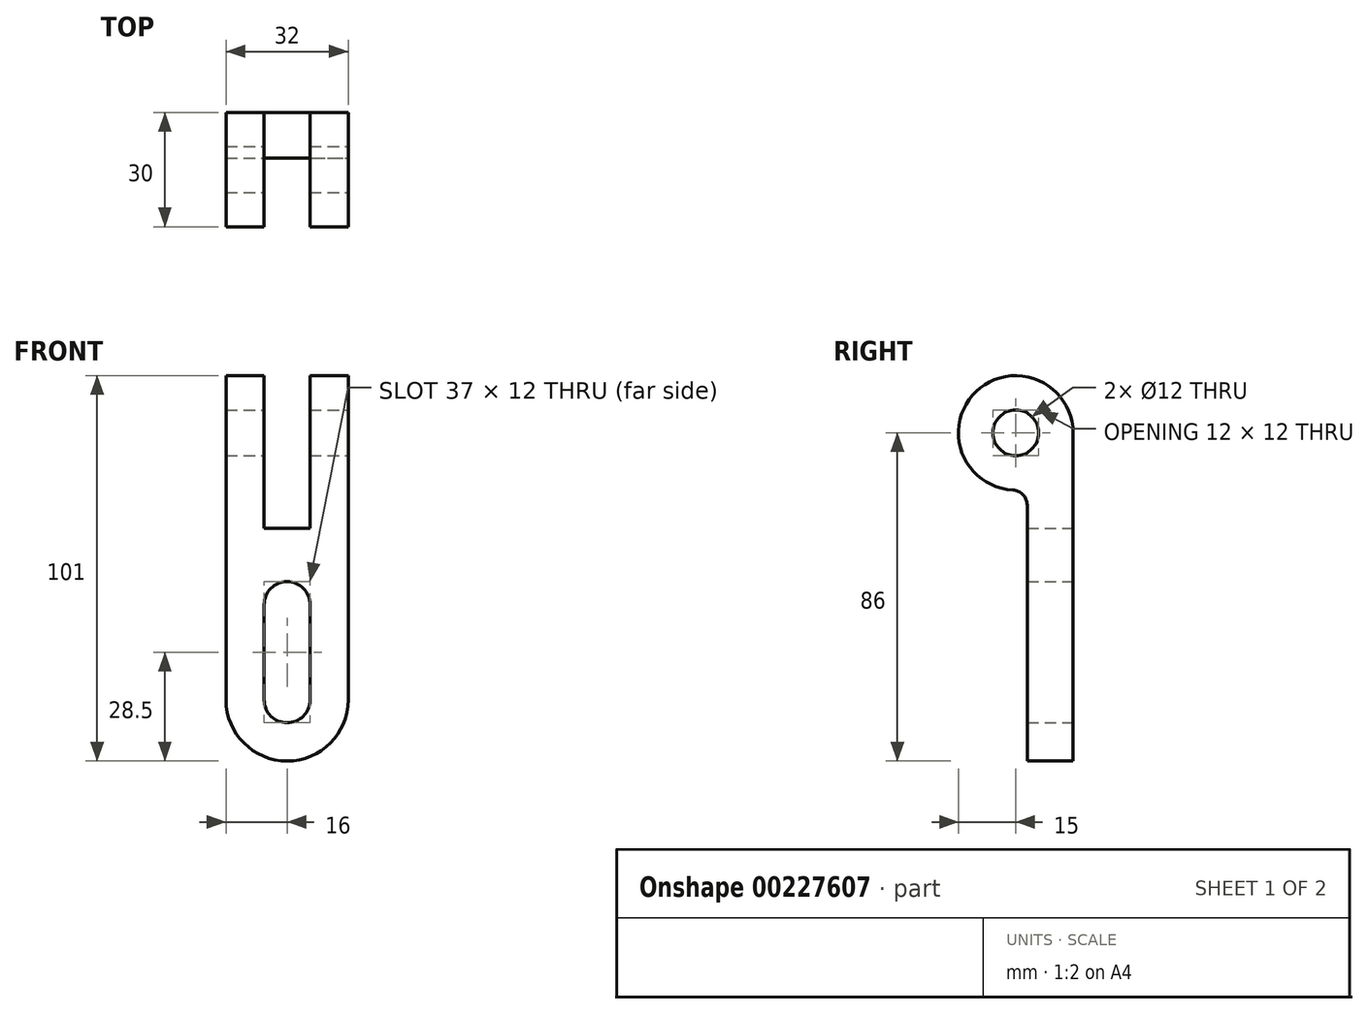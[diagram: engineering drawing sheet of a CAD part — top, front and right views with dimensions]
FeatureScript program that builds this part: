
annotation { "Feature Type Name" : "Feature", "Feature Type Description" : "" }
export const myFeature = defineFeature(function(context is Context, id is Id, definition is map)
    precondition{}
    {
        {
            var Q0;
            Q0=qCreatedBy(makeId("Front.planeOp"),FACE);
            var sketch = newSketch(context, id + "F0", { "sketchPlane" : qUnion([Q0])});
            skArc(sketch, "E0", {"start": v(-16, 0) * mm, "mid": v(-11.31, -11.31) * mm, "end": v(0, -16) * mm});
            skArc(sketch, "E1", {"start": v(-6, 0) * mm, "mid": v(-4.24, -4.24) * mm, "end": v(0, -6) * mm});
            skLineSegment(sketch, "E2", {"start": v(-16, 45) * mm, "end": v(-16, 0) * mm});
            skLineSegment(sketch, "E3", {"start": v(0, -30.56) * mm, "end": v(0, 67.76) * mm, "construction": true});
            skLineSegment(sketch, "E4", {"start": v(-23.42, 0) * mm, "end": v(30.75, 0) * mm, "construction": true});
            skArc(sketch, "E5", {"start": v(0, 31) * mm, "mid": v(-4.24, 29.24) * mm, "end": v(-6, 25) * mm});
            skLineSegment(sketch, "E6", {"start": v(-6, 0) * mm, "end": v(-6, 25) * mm});
            skArc(sketch, "E7.MirrorCS", {"start": v(0, 31) * mm, "mid": v(4.24, 29.24) * mm, "end": v(6, 25) * mm});
            skArc(sketch, "E8.MirrorCS", {"start": v(16, 0) * mm, "mid": v(11.31, -11.31) * mm, "end": v(0, -16) * mm});
            skArc(sketch, "E9.MirrorCS", {"start": v(6, 0) * mm, "mid": v(4.24, -4.24) * mm, "end": v(0, -6) * mm});
            skLineSegment(sketch, "E10.MirrorCS", {"start": v(16, 45) * mm, "end": v(16, 0) * mm});
            skLineSegment(sketch, "E11.MirrorCS", {"start": v(6, 0) * mm, "end": v(6, 25) * mm});
            skLineSegment(sketch, "E12", {"start": v(-16, 45) * mm, "end": v(16, 45) * mm});
            skSolve(sketch);
        }
        {
            var Q0;
            Q0=makeQuery(id+"F0.imprint","IMPRINT",FACE,{"disambiguationData":[TD([[makeQuery(id+"F0.imprint","IMPRINT",EDGE,{"derivedFrom":sQuery(id+"F0.wireOp",EDGE,"E0")}),1.0]])]});
            extrude(context, id + "F1", {"entities" : qUnion([Q0]), "depth" : 12 * mm});
        }
        {
            var Q0;
            Q0=makeQuery(id+"F1.opExtrude","SWEPT_FACE",FACE,{"disambiguationData":[OSD([sQuery(id+"F0.wireOp",EDGE,"E10.MirrorCS")])]});
            var sketch = newSketch(context, id + "F2", { "sketchPlane" : qUnion([Q0])});
            skLineSegment(sketch, "E13", {"start": v(-12, 45) * mm, "end": v(21.97, 45) * mm, "construction": true});
            skLineSegment(sketch, "E14", {"start": v(0, 45) * mm, "end": v(0, 84.89) * mm, "construction": true});
            skLineSegment(sketch, "E15", {"start": v(-15, 90.26) * mm, "end": v(-15, 34.05) * mm, "construction": true});
            skArc(sketch, "E16", {"start": v(0, 70) * mm, "mid": v(-25.32, 80.88) * mm, "end": v(-15.79, 55.02) * mm});
            skCircle(sketch, "E17", {"center": v(-15, 70) * mm, "radius": 6 * mm});
            skLineSegment(sketch, "E18", {"start": v(0, 70) * mm, "end": v(0, 45) * mm});
            skLineSegment(sketch, "E19", {"start": v(-12, 51.03) * mm, "end": v(-12, 45) * mm});
            skArc(sketch, "E20", {"start": v(-12, 51.03) * mm, "mid": v(-13.1, 53.78) * mm, "end": v(-15.79, 55.02) * mm});
            skSolve(sketch);
        }
        {
            var Q0;
            Q0=makeQuery(id+"F2.imprint","IMPRINT",FACE,{"disambiguationData":[TD([[makeQuery(id+"F2.imprint","IMPRINT",EDGE,{"derivedFrom":sQuery(id+"F2.wireOp",EDGE,"E16")}),1.0]])]});
            extrude(context, id + "F3", {"entities" : qUnion([Q0]), "operationType" : NewBodyOperationType.ADD, "oppositeDirection" : true, "depth" : 32 * mm});
        }
        {
            var Q0;
            Q0=makeQuery(id+"F3.boolean.opBoolean","MERGE",FACE,{"derivedFrom":[makeQuery(id+"F1.opExtrude","CAP_FACE",FACE,{"disambiguationData":[OSD([sQuery(id+"F0.wireOp",EDGE,"E0"),sQuery(id+"F0.wireOp",EDGE,"E1"),sQuery(id+"F0.wireOp",EDGE,"E2"),sQuery(id+"F0.wireOp",EDGE,"E5"),sQuery(id+"F0.wireOp",EDGE,"E6"),sQuery(id+"F0.wireOp",EDGE,"E7.MirrorCS"),sQuery(id+"F0.wireOp",EDGE,"E8.MirrorCS"),sQuery(id+"F0.wireOp",EDGE,"E9.MirrorCS"),sQuery(id+"F0.wireOp",EDGE,"E10.MirrorCS"),sQuery(id+"F0.wireOp",EDGE,"E11.MirrorCS"),sQuery(id+"F0.wireOp",EDGE,"E12")])],"isStart":true}),makeQuery(id+"F3.opExtrude","SWEPT_FACE",FACE,{"disambiguationData":[OSD([sQuery(id+"F2.wireOp",EDGE,"E18")])]})]});
            var sketch = newSketch(context, id + "F4", { "sketchPlane" : qUnion([Q0])});
            skLineSegment(sketch, "E21", {"start": v(0, 0) * mm, "end": v(0, 116.81) * mm, "construction": true});
            skLineSegment(sketch, "E22.bottom", {"start": v(-6, 45) * mm, "end": v(6, 45) * mm});
            skLineSegment(sketch, "E22.top", {"start": v(-6, 97) * mm, "end": v(6, 97) * mm});
            skLineSegment(sketch, "E22.left", {"start": v(-6, 45) * mm, "end": v(-6, 97) * mm});
            skLineSegment(sketch, "E22.right", {"start": v(6, 45) * mm, "end": v(6, 97) * mm});
            skSolve(sketch);
        }
        {
            var Q0;
            {var subQ0=sQuery(id+"F4.wireOp",EDGE,"E22.top");Q0=makeQuery(id+"F4.imprint","IMPRINT",FACE,{"disambiguationData":[TD([[makeQuery(id+"F4.imprint","IMPRINT",EDGE,{"derivedFrom":subQ0}),-1.0]])]});}
            var Q1;
            {var subQ0=sQuery(id+"F4.wireOp",EDGE,"E22.bottom");Q1=makeQuery(id+"F4.imprint","IMPRINT",FACE,{"disambiguationData":[TD([[makeQuery(id+"F4.imprint","IMPRINT",EDGE,{"derivedFrom":subQ0}),1.0]])]});}
            extrude(context, id + "F5", {"entities" : qUnion([Q0, Q1]), "operationType" : NewBodyOperationType.REMOVE, "endBound" : BoundingType.THROUGH_ALL, "oppositeDirection" : true, "depth" : 25 * mm});
        }
    });
